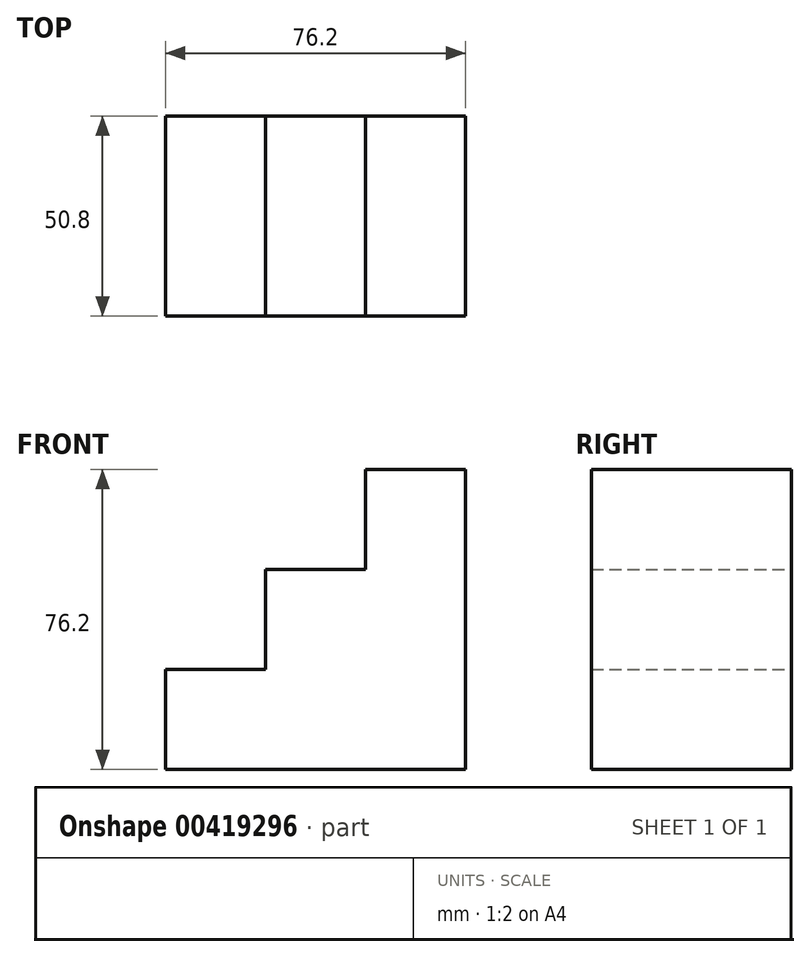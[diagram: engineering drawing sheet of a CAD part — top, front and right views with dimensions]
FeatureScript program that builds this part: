
annotation { "Feature Type Name" : "Feature", "Feature Type Description" : "" }
export const myFeature = defineFeature(function(context is Context, id is Id, definition is map)
    precondition{}
    {
        {
            var Q0;
            Q0=qCreatedBy(makeId("Front.planeOp"),FACE);
            var sketch = newSketch(context, id + "F0", { "sketchPlane" : qUnion([Q0])});
            skLineSegment(sketch, "E0", {"start": v(-43.1, 0) * mm, "end": v(33.1, 0) * mm});
            skLineSegment(sketch, "E1", {"start": v(33.1, 0) * mm, "end": v(33.1, 76.2) * mm});
            skLineSegment(sketch, "E2", {"start": v(33.1, 76.2) * mm, "end": v(7.7, 76.2) * mm});
            skLineSegment(sketch, "E3", {"start": v(7.7, 76.2) * mm, "end": v(7.7, 50.8) * mm});
            skLineSegment(sketch, "E4", {"start": v(7.7, 50.8) * mm, "end": v(-17.7, 50.8) * mm});
            skLineSegment(sketch, "E5", {"start": v(-17.7, 50.8) * mm, "end": v(-17.7, 25.4) * mm});
            skLineSegment(sketch, "E6", {"start": v(-17.7, 25.4) * mm, "end": v(-43.1, 25.4) * mm});
            skLineSegment(sketch, "E7", {"start": v(-43.1, 25.4) * mm, "end": v(-43.1, 0) * mm});
            skSolve(sketch);
        }
        {
            var Q0;
            Q0 = qSketchRegion(id + "F0", true);
            extrude(context, id + "F1", {"entities" : qUnion([Q0]), "depth" : 50.8 * mm});
        }
    });
